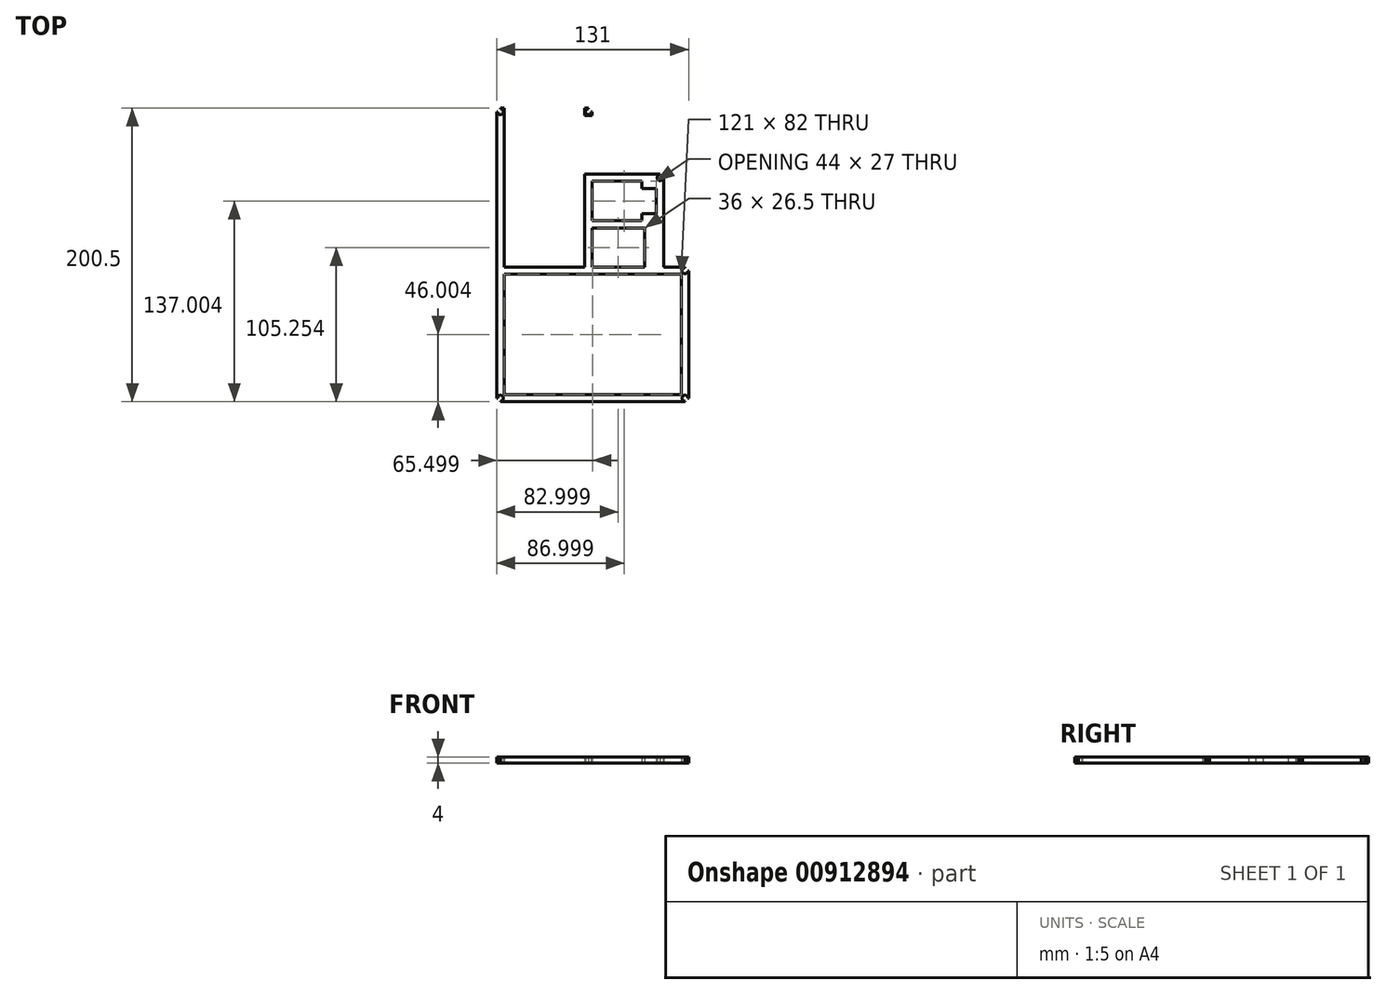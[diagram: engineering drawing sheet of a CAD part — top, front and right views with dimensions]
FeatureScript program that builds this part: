
annotation { "Feature Type Name" : "Feature", "Feature Type Description" : "" }
export const myFeature = defineFeature(function(context is Context, id is Id, definition is map)
    precondition{}
    {
        {
            var Q0;
            Q0=qCreatedBy(makeId("Top.planeOp"),FACE);
            var sketch = newSketch(context, id + "F0", { "sketchPlane" : qUnion([Q0])});
            skLineSegment(sketch, "E0.bottom", {"start": v(-40.7, -58.83) * mm, "end": v(14.3, -58.83) * mm});
            skLineSegment(sketch, "E0.top", {"start": v(-40.7, 44.67) * mm, "end": v(14.3, 44.67) * mm});
            skLineSegment(sketch, "E0.left", {"start": v(-40.7, -58.83) * mm, "end": v(-40.7, 44.67) * mm});
            skLineSegment(sketch, "E0.right", {"start": v(14.3, -58.83) * mm, "end": v(14.3, 44.67) * mm});
            skLineSegment(sketch, "E1.bottom", {"start": v(-45.7, 49.67) * mm, "end": v(85.3, 49.67) * mm});
            skLineSegment(sketch, "E1.top", {"start": v(-45.7, -150.83) * mm, "end": v(85.3, -150.83) * mm});
            skLineSegment(sketch, "E1.left", {"start": v(-45.7, 49.67) * mm, "end": v(-45.7, -150.83) * mm});
            skLineSegment(sketch, "E1.right", {"start": v(85.3, 49.67) * mm, "end": v(85.3, -150.83) * mm});
            skLineSegment(sketch, "E2.bottom", {"start": v(-40.7, -63.83) * mm, "end": v(80.3, -63.83) * mm});
            skLineSegment(sketch, "E2.top", {"start": v(-40.7, -145.83) * mm, "end": v(80.3, -145.83) * mm});
            skLineSegment(sketch, "E2.left", {"start": v(-40.7, -63.83) * mm, "end": v(-40.7, -145.83) * mm});
            skLineSegment(sketch, "E2.right", {"start": v(80.3, -63.83) * mm, "end": v(80.3, -145.83) * mm});
            skLineSegment(sketch, "E3.top", {"start": v(14.3, -63.83) * mm, "end": v(19.3, -63.83) * mm});
            skLineSegment(sketch, "E4.bottom", {"start": v(19.3, -58.83) * mm, "end": v(55.3, -58.83) * mm});
            skLineSegment(sketch, "E4.top", {"start": v(19.3, -32.33) * mm, "end": v(55.3, -32.33) * mm});
            skLineSegment(sketch, "E4.left", {"start": v(19.3, -58.83) * mm, "end": v(19.3, -32.33) * mm});
            skLineSegment(sketch, "E4.right", {"start": v(55.3, -58.83) * mm, "end": v(55.3, -32.33) * mm});
            skLineSegment(sketch, "E5.right", {"start": v(14.3, -32.33) * mm, "end": v(14.3, -27.33) * mm});
            skLineSegment(sketch, "E6.bottom", {"start": v(19.3, -27.33) * mm, "end": v(53.3, -27.33) * mm});
            skLineSegment(sketch, "E6.top", {"start": v(19.3, -0.33) * mm, "end": v(53.3, -0.33) * mm});
            skLineSegment(sketch, "E6.left", {"start": v(19.3, -27.33) * mm, "end": v(19.3, -0.33) * mm});
            skLineSegment(sketch, "E6.right", {"start": v(53.3, -27.33) * mm, "end": v(53.3, -0.33) * mm});
            skLineSegment(sketch, "E7", {"start": v(53.3, -27.33) * mm, "end": v(53.3, -22.33) * mm});
            skLineSegment(sketch, "E8", {"start": v(53.3, -22.33) * mm, "end": v(53.3, -5.33) * mm});
            skLineSegment(sketch, "E9.bottom", {"start": v(53.3, -5.33) * mm, "end": v(53.3, -5.33) * mm});
            skLineSegment(sketch, "E9.top", {"start": v(53.3, -22.33) * mm, "end": v(53.3, -22.33) * mm});
            skLineSegment(sketch, "E9.left", {"start": v(53.3, -5.33) * mm, "end": v(53.3, -22.33) * mm});
            skLineSegment(sketch, "E9.right", {"start": v(53.3, -5.33) * mm, "end": v(53.3, -22.33) * mm});
            skLineSegment(sketch, "E10.bottom", {"start": v(53.3, -22.33) * mm, "end": v(63.3, -22.33) * mm});
            skLineSegment(sketch, "E10.top", {"start": v(53.3, -5.33) * mm, "end": v(63.3, -5.33) * mm});
            skLineSegment(sketch, "E10.right", {"start": v(63.3, -22.33) * mm, "end": v(63.3, -5.33) * mm});
            skLineSegment(sketch, "E11.bottom", {"start": v(14.3, 44.67) * mm, "end": v(19.3, 44.67) * mm});
            skLineSegment(sketch, "E11.top", {"start": v(14.3, 49.67) * mm, "end": v(19.3, 49.67) * mm});
            skLineSegment(sketch, "E11.left", {"start": v(14.3, 44.67) * mm, "end": v(14.3, 49.67) * mm});
            skLineSegment(sketch, "E11.right", {"start": v(19.3, 44.67) * mm, "end": v(19.3, 49.67) * mm});
            skLineSegment(sketch, "E12.bottom", {"start": v(19.3, -0.33) * mm, "end": v(14.3, -0.33) * mm});
            skLineSegment(sketch, "E12.top", {"start": v(19.3, 4.67) * mm, "end": v(14.3, 4.67) * mm});
            skLineSegment(sketch, "E12.left", {"start": v(19.3, -0.33) * mm, "end": v(19.3, 4.67) * mm});
            skLineSegment(sketch, "E12.right", {"start": v(14.3, -0.33) * mm, "end": v(14.3, 4.67) * mm});
            skLineSegment(sketch, "E13.bottom", {"start": v(85.3, 49.67) * mm, "end": v(80.3, 49.67) * mm});
            skLineSegment(sketch, "E13.left", {"start": v(85.3, 49.67) * mm, "end": v(85.3, 44.67) * mm});
            skLineSegment(sketch, "E14.top", {"start": v(19.3, 49.67) * mm, "end": v(85.3, 49.67) * mm});
            skLineSegment(sketch, "E14.left", {"start": v(19.3, 4.67) * mm, "end": v(19.3, 49.67) * mm});
            skLineSegment(sketch, "E14.right", {"start": v(85.3, 4.67) * mm, "end": v(85.3, 49.67) * mm});
            skLineSegment(sketch, "E15.bottom", {"start": v(80.3, -63.83) * mm, "end": v(85.3, -63.83) * mm});
            skLineSegment(sketch, "E15.top", {"start": v(80.3, -58.83) * mm, "end": v(85.3, -58.83) * mm});
            skLineSegment(sketch, "E15.left", {"start": v(80.3, -63.83) * mm, "end": v(80.3, -58.83) * mm});
            skLineSegment(sketch, "E15.right", {"start": v(85.3, -63.83) * mm, "end": v(85.3, -58.83) * mm});
            skLineSegment(sketch, "E16", {"start": v(63.3, -5.33) * mm, "end": v(68.3, -5.33) * mm});
            skLineSegment(sketch, "E17", {"start": v(68.3, -5.33) * mm, "end": v(68.3, -22.33) * mm});
            skLineSegment(sketch, "E18.bottom", {"start": v(85.3, -58.83) * mm, "end": v(68.3, -58.83) * mm});
            skLineSegment(sketch, "E18.left", {"start": v(85.3, -58.83) * mm, "end": v(85.3, 4.67) * mm});
            skLineSegment(sketch, "E18.right", {"start": v(68.3, -58.83) * mm, "end": v(68.3, 4.67) * mm});
            skLineSegment(sketch, "E19", {"start": v(19.3, 4.67) * mm, "end": v(68.3, 4.67) * mm});
            skLineSegment(sketch, "E20.bottom", {"start": v(68.3, 4.67) * mm, "end": v(65.8, 4.67) * mm});
            skLineSegment(sketch, "E20.top", {"start": v(68.3, 2.17) * mm, "end": v(65.8, 2.17) * mm});
            skLineSegment(sketch, "E20.left", {"start": v(68.3, 4.67) * mm, "end": v(68.3, 2.17) * mm});
            skLineSegment(sketch, "E20.right", {"start": v(65.8, 4.67) * mm, "end": v(65.8, 2.17) * mm});
            skLineSegment(sketch, "E21.bottom", {"start": v(19.3, 44.67) * mm, "end": v(16.8, 44.67) * mm});
            skLineSegment(sketch, "E21.top", {"start": v(19.3, 47.17) * mm, "end": v(16.8, 47.17) * mm});
            skLineSegment(sketch, "E21.left", {"start": v(19.3, 44.67) * mm, "end": v(19.3, 47.17) * mm});
            skLineSegment(sketch, "E22.bottom", {"start": v(85.3, -58.83) * mm, "end": v(82.8, -58.83) * mm});
            skLineSegment(sketch, "E22.top", {"start": v(85.3, -61.33) * mm, "end": v(82.8, -61.33) * mm});
            skLineSegment(sketch, "E22.left", {"start": v(85.3, -58.83) * mm, "end": v(85.3, -61.33) * mm});
            skLineSegment(sketch, "E22.right", {"start": v(82.8, -58.83) * mm, "end": v(82.8, -61.33) * mm});
            skLineSegment(sketch, "E23.bottom", {"start": v(85.3, -150.83) * mm, "end": v(82.8, -150.83) * mm});
            skLineSegment(sketch, "E23.top", {"start": v(85.3, -148.33) * mm, "end": v(82.8, -148.33) * mm});
            skLineSegment(sketch, "E23.left", {"start": v(85.3, -150.83) * mm, "end": v(85.3, -148.33) * mm});
            skLineSegment(sketch, "E23.right", {"start": v(82.8, -150.83) * mm, "end": v(82.8, -148.33) * mm});
            skLineSegment(sketch, "E24.bottom", {"start": v(-45.7, -150.83) * mm, "end": v(-43.2, -150.83) * mm});
            skLineSegment(sketch, "E24.top", {"start": v(-45.7, -148.33) * mm, "end": v(-43.2, -148.33) * mm});
            skLineSegment(sketch, "E24.left", {"start": v(-45.7, -150.83) * mm, "end": v(-45.7, -148.33) * mm});
            skLineSegment(sketch, "E24.right", {"start": v(-43.2, -150.83) * mm, "end": v(-43.2, -148.33) * mm});
            skLineSegment(sketch, "E25.bottom", {"start": v(-45.7, 49.67) * mm, "end": v(-43.2, 49.67) * mm});
            skLineSegment(sketch, "E25.top", {"start": v(-45.7, 47.17) * mm, "end": v(-43.2, 47.17) * mm});
            skLineSegment(sketch, "E25.left", {"start": v(-45.7, 49.67) * mm, "end": v(-45.7, 47.17) * mm});
            skLineSegment(sketch, "E25.right", {"start": v(-43.2, 49.67) * mm, "end": v(-43.2, 47.17) * mm});
            skLineSegment(sketch, "E26.bottom", {"start": v(19.3, 49.67) * mm, "end": v(16.8, 49.67) * mm});
            skLineSegment(sketch, "E26.left", {"start": v(19.3, 49.67) * mm, "end": v(19.3, 47.17) * mm});
            skLineSegment(sketch, "E26.right", {"start": v(16.8, 49.67) * mm, "end": v(16.8, 47.17) * mm});
            skCircle(sketch, "E27", {"center": v(16.8, 47.17) * mm, "radius": 2 * mm});
            skCircle(sketch, "E28", {"center": v(65.8, 2.17) * mm, "radius": 2 * mm});
            skCircle(sketch, "E29", {"center": v(82.8, -61.33) * mm, "radius": 2 * mm});
            skCircle(sketch, "E30", {"center": v(82.8, -148.33) * mm, "radius": 2 * mm});
            skCircle(sketch, "E31", {"center": v(-43.2, -148.33) * mm, "radius": 2 * mm});
            skCircle(sketch, "E32", {"center": v(-43.2, 47.17) * mm, "radius": 2 * mm});
            skLineSegment(sketch, "E33.bottom", {"start": v(-40.7, -63.83) * mm, "end": v(-37.3, -63.83) * mm});
            skLineSegment(sketch, "E33.top", {"start": v(-40.7, -67.23) * mm, "end": v(-37.3, -67.23) * mm});
            skLineSegment(sketch, "E33.left", {"start": v(-40.7, -63.83) * mm, "end": v(-40.7, -67.23) * mm});
            skLineSegment(sketch, "E33.right", {"start": v(-37.3, -63.83) * mm, "end": v(-37.3, -67.23) * mm});
            skLineSegment(sketch, "E34.bottom", {"start": v(-40.7, -145.83) * mm, "end": v(-37.3, -145.83) * mm});
            skLineSegment(sketch, "E34.top", {"start": v(-40.7, -142.43) * mm, "end": v(-37.3, -142.43) * mm});
            skLineSegment(sketch, "E34.left", {"start": v(-40.7, -145.83) * mm, "end": v(-40.7, -142.43) * mm});
            skLineSegment(sketch, "E34.right", {"start": v(-37.3, -145.83) * mm, "end": v(-37.3, -142.43) * mm});
            skLineSegment(sketch, "E35.bottom", {"start": v(80.3, -145.83) * mm, "end": v(76.9, -145.83) * mm});
            skLineSegment(sketch, "E35.top", {"start": v(80.3, -142.43) * mm, "end": v(76.9, -142.43) * mm});
            skLineSegment(sketch, "E35.left", {"start": v(80.3, -145.83) * mm, "end": v(80.3, -142.43) * mm});
            skLineSegment(sketch, "E35.right", {"start": v(76.9, -145.83) * mm, "end": v(76.9, -142.43) * mm});
            skLineSegment(sketch, "E36.bottom", {"start": v(80.3, -63.83) * mm, "end": v(76.9, -63.83) * mm});
            skLineSegment(sketch, "E36.top", {"start": v(80.3, -67.23) * mm, "end": v(76.9, -67.23) * mm});
            skLineSegment(sketch, "E36.left", {"start": v(80.3, -63.83) * mm, "end": v(80.3, -67.23) * mm});
            skLineSegment(sketch, "E36.right", {"start": v(76.9, -63.83) * mm, "end": v(76.9, -67.23) * mm});
            skLineSegment(sketch, "E37.bottom", {"start": v(-40.7, -58.83) * mm, "end": v(-37.7, -58.83) * mm});
            skLineSegment(sketch, "E37.top", {"start": v(-40.7, 28.47) * mm, "end": v(-37.7, 28.47) * mm});
            skLineSegment(sketch, "E37.left", {"start": v(-40.7, -58.83) * mm, "end": v(-40.7, 28.47) * mm});
            skLineSegment(sketch, "E37.right", {"start": v(-37.7, -58.83) * mm, "end": v(-37.7, 28.47) * mm});
            skLineSegment(sketch, "E38.bottom", {"start": v(-37.7, -58.83) * mm, "end": v(-40.7, -58.83) * mm});
            skLineSegment(sketch, "E38.top", {"start": v(-37.7, -52.83) * mm, "end": v(-40.7, -52.83) * mm});
            skLineSegment(sketch, "E38.left", {"start": v(-37.7, -58.83) * mm, "end": v(-37.7, -52.83) * mm});
            skLineSegment(sketch, "E38.right", {"start": v(-40.7, -58.83) * mm, "end": v(-40.7, -52.83) * mm});
            skLineSegment(sketch, "E39.bottom", {"start": v(14.3, -58.83) * mm, "end": v(11.3, -58.83) * mm});
            skLineSegment(sketch, "E39.top", {"start": v(14.3, 29.87) * mm, "end": v(11.3, 29.87) * mm});
            skLineSegment(sketch, "E39.left", {"start": v(14.3, -58.83) * mm, "end": v(14.3, 29.87) * mm});
            skLineSegment(sketch, "E39.right", {"start": v(11.3, -58.83) * mm, "end": v(11.3, 29.87) * mm});
            skLineSegment(sketch, "E40.top", {"start": v(14.3, -47.23) * mm, "end": v(11.3, -47.23) * mm});
            skLineSegment(sketch, "E40.left", {"start": v(14.3, -58.83) * mm, "end": v(14.3, -47.23) * mm});
            skLineSegment(sketch, "E40.right", {"start": v(11.3, -58.83) * mm, "end": v(11.3, -47.23) * mm});
            skCircle(sketch, "E41", {"center": v(-37.7, -52.83) * mm, "radius": 2 * mm});
            skCircle(sketch, "E42", {"center": v(-37.7, 28.47) * mm, "radius": 2 * mm});
            skCircle(sketch, "E43", {"center": v(11.3, 29.87) * mm, "radius": 2 * mm});
            skCircle(sketch, "E44", {"center": v(11.3, -47.23) * mm, "radius": 2 * mm});
            skLineSegment(sketch, "E45.bottom", {"start": v(19.3, -0.33) * mm, "end": v(28.55, -0.33) * mm});
            skLineSegment(sketch, "E45.top", {"start": v(19.3, -2.28) * mm, "end": v(28.55, -2.28) * mm});
            skLineSegment(sketch, "E45.left", {"start": v(19.3, -0.33) * mm, "end": v(19.3, -2.28) * mm});
            skLineSegment(sketch, "E45.right", {"start": v(28.55, -0.33) * mm, "end": v(28.55, -2.28) * mm});
            skLineSegment(sketch, "E46.bottom", {"start": v(19.3, -27.33) * mm, "end": v(28.55, -27.33) * mm});
            skLineSegment(sketch, "E46.top", {"start": v(19.3, -25.38) * mm, "end": v(28.55, -25.38) * mm});
            skLineSegment(sketch, "E46.left", {"start": v(19.3, -27.33) * mm, "end": v(19.3, -25.38) * mm});
            skLineSegment(sketch, "E46.right", {"start": v(28.55, -27.33) * mm, "end": v(28.55, -25.38) * mm});
            skLineSegment(sketch, "E47.bottom", {"start": v(53.3, -0.33) * mm, "end": v(51.35, -0.33) * mm});
            skLineSegment(sketch, "E47.top", {"start": v(53.3, -2.28) * mm, "end": v(51.35, -2.28) * mm});
            skLineSegment(sketch, "E47.left", {"start": v(53.3, -0.33) * mm, "end": v(53.3, -2.28) * mm});
            skLineSegment(sketch, "E47.right", {"start": v(51.35, -0.33) * mm, "end": v(51.35, -2.28) * mm});
            skLineSegment(sketch, "E48.bottom", {"start": v(53.3, -27.33) * mm, "end": v(51.35, -27.33) * mm});
            skLineSegment(sketch, "E48.top", {"start": v(53.3, -25.38) * mm, "end": v(51.35, -25.38) * mm});
            skLineSegment(sketch, "E48.left", {"start": v(53.3, -27.33) * mm, "end": v(53.3, -25.38) * mm});
            skLineSegment(sketch, "E48.right", {"start": v(51.35, -27.33) * mm, "end": v(51.35, -25.38) * mm});
            skLineSegment(sketch, "E49.bottom", {"start": v(55.3, -32.33) * mm, "end": v(53.6, -32.33) * mm});
            skLineSegment(sketch, "E49.top", {"start": v(55.3, -34.03) * mm, "end": v(53.6, -34.03) * mm});
            skLineSegment(sketch, "E49.left", {"start": v(55.3, -32.33) * mm, "end": v(55.3, -34.03) * mm});
            skLineSegment(sketch, "E49.right", {"start": v(53.6, -32.33) * mm, "end": v(53.6, -34.03) * mm});
            skLineSegment(sketch, "E50.bottom", {"start": v(55.3, -58.83) * mm, "end": v(53.6, -58.83) * mm});
            skLineSegment(sketch, "E50.top", {"start": v(55.3, -57.13) * mm, "end": v(53.6, -57.13) * mm});
            skLineSegment(sketch, "E50.left", {"start": v(55.3, -58.83) * mm, "end": v(55.3, -57.13) * mm});
            skLineSegment(sketch, "E50.right", {"start": v(53.6, -58.83) * mm, "end": v(53.6, -57.13) * mm});
            skCircle(sketch, "E51", {"center": v(53.6, -34.03) * mm, "radius": 1.2 * mm});
            skCircle(sketch, "E52", {"center": v(53.6, -57.13) * mm, "radius": 1.2 * mm});
            skCircle(sketch, "E53", {"center": v(51.35, -25.38) * mm, "radius": 1.15 * mm});
            skCircle(sketch, "E54", {"center": v(28.55, -25.38) * mm, "radius": 1.15 * mm});
            skCircle(sketch, "E55", {"center": v(28.55, -2.28) * mm, "radius": 1.15 * mm});
            skCircle(sketch, "E56", {"center": v(51.35, -2.28) * mm, "radius": 1.15 * mm});
            skCircle(sketch, "E57", {"center": v(-37.3, -67.23) * mm, "radius": 1.4 * mm});
            skCircle(sketch, "E58", {"center": v(76.9, -67.23) * mm, "radius": 1.4 * mm});
            skCircle(sketch, "E59", {"center": v(-37.3, -142.43) * mm, "radius": 1.4 * mm});
            skCircle(sketch, "E60", {"center": v(76.9, -142.43) * mm, "radius": 1.4 * mm});
            skLineSegment(sketch, "E61.bottom", {"start": v(-40.7, 44.67) * mm, "end": v(-35.7, 44.67) * mm});
            skLineSegment(sketch, "E61.top", {"start": v(-40.7, 49.67) * mm, "end": v(-35.7, 49.67) * mm});
            skLineSegment(sketch, "E61.left", {"start": v(-40.7, 44.67) * mm, "end": v(-40.7, 49.67) * mm});
            skLineSegment(sketch, "E61.right", {"start": v(-35.7, 44.67) * mm, "end": v(-35.7, 49.67) * mm});
            skLineSegment(sketch, "E62.bottom", {"start": v(14.3, 44.67) * mm, "end": v(9.3, 44.67) * mm});
            skLineSegment(sketch, "E62.top", {"start": v(14.3, 49.67) * mm, "end": v(9.3, 49.67) * mm});
            skLineSegment(sketch, "E62.right", {"start": v(9.3, 44.67) * mm, "end": v(9.3, 49.67) * mm});
            skSolve(sketch);
        }
        {
            var Q0;
            {var subQ1=sQuery(id+"F0.wireOp",EDGE,"E23.bottom");Q0=makeQuery(id+"F0.imprint","IMPRINT",FACE,{"disambiguationData":[TD([[makeQuery(id+"F0.imprint","IMPRINT",EDGE,{"derivedFrom":subQ1}),-1.0]])]});}
            var Q1;
            {var subQ1=sQuery(id+"F0.wireOp",EDGE,"E24.bottom");Q1=makeQuery(id+"F0.imprint","IMPRINT",FACE,{"disambiguationData":[TD([[makeQuery(id+"F0.imprint","IMPRINT",EDGE,{"derivedFrom":subQ1}),1.0]])]});}
            var Q2;
            {var subQ1=sQuery(id+"F0.wireOp",EDGE,"E25.bottom");Q2=makeQuery(id+"F0.imprint","IMPRINT",FACE,{"disambiguationData":[TD([[makeQuery(id+"F0.imprint","IMPRINT",EDGE,{"derivedFrom":subQ1}),-1.0]])]});}
            var Q3;
            {var subQ1=sQuery(id+"F0.wireOp",EDGE,"E22.bottom");Q3=makeQuery(id+"F0.imprint","IMPRINT",FACE,{"disambiguationData":[TD([[makeQuery(id+"F0.imprint","IMPRINT",EDGE,{"derivedFrom":subQ1}),1.0]])]});}
            var Q4;
            {var subQ1=sQuery(id+"F0.wireOp",EDGE,"E26.bottom");Q4=makeQuery(id+"F0.imprint","IMPRINT",FACE,{"disambiguationData":[TD([[makeQuery(id+"F0.imprint","IMPRINT",EDGE,{"derivedFrom":subQ1}),1.0]])]});}
            var Q5;
            Q5=makeQuery(id+"F0.imprint","IMPRINT",FACE,{"disambiguationData":[TD([[makeQuery(id+"F0.imprint","IMPRINT",EDGE,{"derivedFrom":sQuery(id+"F0.wireOp",EDGE,"E15.bottom")}),1.0]])]});
            var Q6;
            Q6=makeQuery(id+"F0.imprint","IMPRINT",FACE,{"disambiguationData":[TD([[makeQuery(id+"F0.imprint","IMPRINT",EDGE,{"derivedFrom":sQuery(id+"F0.wireOp",EDGE,"E11.bottom")}),1.0]])]});
            var Q7;
            Q7=makeQuery(id+"F0.imprint","IMPRINT",FACE,{"disambiguationData":[TD([[makeQuery(id+"F0.imprint","IMPRINT",EDGE,{"derivedFrom":sQuery(id+"F0.wireOp",EDGE,"E0.bottom")}),-1.0]])]});
            var Q8;
            {var subQ0=sQuery(id+"F0.wireOp",EDGE,"E12.bottom");Q8=makeQuery(id+"F0.imprint","IMPRINT",FACE,{"disambiguationData":[TD([[makeQuery(id+"F0.imprint","IMPRINT",EDGE,{"derivedFrom":subQ0}),-1.0]])]});}
            var Q9;
            {var subQ1=sQuery(id+"F0.wireOp",EDGE,"E0.right");Q9=makeQuery(id+"F0.imprint","IMPRINT",FACE,{"disambiguationData":[TD([[makeQuery(id+"F0.imprint","IMPRINT",EDGE,{"derivedFrom":subQ1}),-1.0]])]});}
            var Q10;
            Q10=makeQuery(id+"F0.imprint","IMPRINT",FACE,{"disambiguationData":[TD([[makeQuery(id+"F0.imprint","IMPRINT",EDGE,{"derivedFrom":sQuery(id+"F0.wireOp",EDGE,"E6.top")}),1.0]])]});
            var Q11;
            {var subQ1=sQuery(id+"F0.wireOp",EDGE,"E20.bottom");Q11=makeQuery(id+"F0.imprint","IMPRINT",FACE,{"disambiguationData":[TD([[makeQuery(id+"F0.imprint","IMPRINT",EDGE,{"derivedFrom":subQ1}),1.0]])]});}
            var Q12;
            Q12=makeQuery(id+"F0.imprint","IMPRINT",FACE,{"disambiguationData":[TD([[makeQuery(id+"F0.imprint","IMPRINT",EDGE,{"derivedFrom":sQuery(id+"F0.wireOp",EDGE,"E61.bottom")}),1.0]])]});
            var Q13;
            Q13=makeQuery(id+"F0.imprint","IMPRINT",FACE,{"disambiguationData":[TD([[makeQuery(id+"F0.imprint","IMPRINT",EDGE,{"derivedFrom":sQuery(id+"F0.wireOp",EDGE,"E62.bottom")}),-1.0]])]});
            extrude(context, id + "F1", {"entities" : qUnion([Q0, Q1, Q2, Q3, Q4, Q5, Q6, Q7, Q8, Q9, Q10, Q11, Q12, Q13]), "depth" : 4 * mm, "offsetDistance" : 25 * mm});
        }
    });
